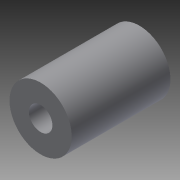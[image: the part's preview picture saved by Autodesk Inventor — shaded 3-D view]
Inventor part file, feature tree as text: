
AUTODESK INVENTOR PART (.ipt)
format: ipt  version: 2015 (Build 190159000, 159)  size: 93,184 bytes
history: native  units: mm
features: extrude x3, sketch x3
ambient origin geometry x8: Origin, YZ Plane, XZ Plane, XY Plane, X Axis, Y Axis, Z Axis, Center Point
bodies: Solid1 (feature_tree)
feature tree (6):
  extrude  "Extrusion1"  Depth=25.4mm TaperAngle=0.0deg
  extrude  "Extrusion2"  Depth=3.22mm
  extrude  "Extrusion3"  Depth=12.7mm TaperAngle=0.0deg
  sketch  "Sketch1"  dims[d0=16.0mm d1=25.4mm d2=0.0mm]
  sketch  "Sketch3"  dims[d13=3.22mm d15=1.61mm]
  sketch  "Sketch4"  dims[d16=1.61mm d17=12.7mm d18=0.0mm d19=6.05mm d20=12.7mm d21=0.0mm]
